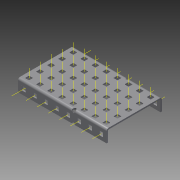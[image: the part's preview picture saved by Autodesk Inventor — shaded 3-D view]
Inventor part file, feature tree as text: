
AUTODESK INVENTOR PART (.ipt)
format: ipt  version: 2015 (Build 190159000, 159)  size: 2,488,320 bytes
history: native  units: in
note: dims shown in document units (in); Inventor stores cm internally (conversion verified against a paired STEP export)
features: other x62, pattern_linear x2, sheet_metal_op x1, extrude x1, imported_body x1, sketch x1
ambient origin geometry x8: Origin, YZ Plane, XZ Plane, XY Plane, X Axis, Y Axis, Z Axis, Center Point
bodies: Body1 (feature_tree)
feature tree (68):
  sheet_metal_op  "Fold1"
  other  "C-Channel"
  extrude  "length cut"  Depth=0.5in
  other  "top axis"
  other  "front axis"
  other  "back axis"
  pattern_linear  "top axes"  Spacing1=0.5in  [1 undecoded]
  pattern_linear  "horiz axes"  Spacing1=0.0in  [1 undecoded]
  other  "right plane"
  imported_body  "Base1"
  sketch  "Sketch1"  dims[d1=0.0in d4=0.5in d5=1.9685in d7=0.5in d10=0.5in d11=0.0in d12=0.0in d13=0.0in d14=-4.0in d15=0.0in d16=0.0in]
  other  "Work Point1"
  other  "Work Axis6"
  other  "Work Axis11"
  other  "Work Axis16"
  other  "Work Axis21"
  other  "Work Point2"
  other  "Work Point3"
  other  "Work Axis36"
  other  "Work Axis37"
  other  "Work Axis38"
  other  "Work Axis39"
  other  "Work Axis40"
  other  "Work Axis41"
  other  "Work Axis60"
  other  "Work Axis61"
  other  "Work Axis62"
  other  "Work Axis63"
  other  "Work Axis64"
  other  "Work Axis65"
  other  "Work Axis84"
  other  "Work Axis85"
  other  "Work Axis86"
  other  "Work Axis87"
  other  "Work Axis88"
  other  "Work Axis89"
  other  "Work Axis108"
  other  "Work Axis109"
  other  "Work Axis110"
  other  "Work Axis111"
  other  "Work Axis112"
  other  "Work Axis113"
  other  "Work Axis132"
  other  "Work Axis133"
  other  "Work Axis134"
  other  "Work Axis135"
  other  "Work Axis136"
  other  "Work Axis137"
  other  "Work Axis156"
  other  "Work Axis157"
  other  "Work Axis158"
  other  "Work Axis159"
  other  "Work Axis160"
  other  "Work Axis161"
  other  "Work Axis180"
  other  "Work Axis181"
  other  "Work Axis182"
  other  "Work Axis183"
  other  "Work Axis184"
  other  "Work Axis185"
  other  "Work Axis204"
  other  "Work Axis232"
  other  "Work Axis260"
  other  "Work Axis288"
  other  "Work Axis316"
  other  "Work Axis344"
  other  "Work Axis372"
  other  "left plane"
note: 2 required parameter values undecoded (feature->parameter linkage not recoverable at this tier; creation-order binding heuristic only, values carry confidence <= 0.55)
